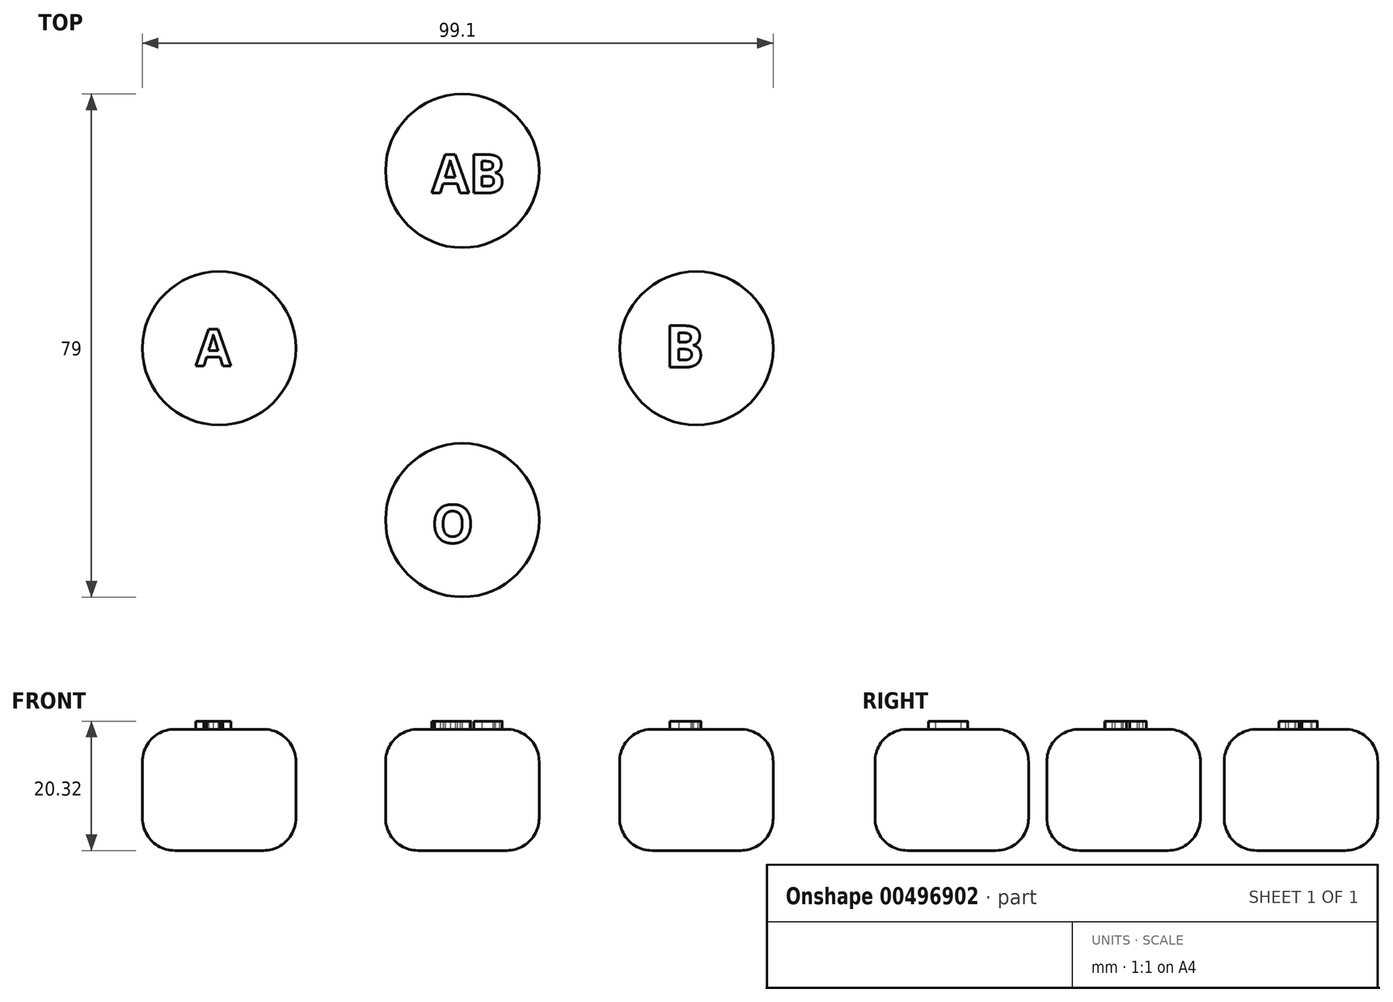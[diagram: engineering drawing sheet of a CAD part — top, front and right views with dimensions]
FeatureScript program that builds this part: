
annotation { "Feature Type Name" : "Feature", "Feature Type Description" : "" }
export const myFeature = defineFeature(function(context is Context, id is Id, definition is map)
    precondition{}
    {
        {
            var Q0;
            Q0=qCreatedBy(makeId("Top.planeOp"),FACE);
            var sketch = newSketch(context, id + "F0", { "sketchPlane" : qUnion([Q0])});
            skCircle(sketch, "E0", {"center": v(0, -27) * mm, "radius": 12.07 * mm});
            skCircle(sketch, "E1", {"center": v(36.77, 0) * mm, "radius": 12.07 * mm});
            skCircle(sketch, "E2", {"center": v(0, 27.86) * mm, "radius": 12.07 * mm});
            skCircle(sketch, "E3", {"center": v(-38.2, 0) * mm, "radius": 12.07 * mm});
            skSolve(sketch);
        }
        {
            var Q0;
            Q0 = qSketchRegion(id + "F0", true);
            extrude(context, id + "F1", {"entities" : qUnion([Q0]), "depth" : 19.05 * mm});
        }
        {
            var Q0;
            Q0=makeQuery(id+"F1.opExtrude","CAP_EDGE",EDGE,{"disambiguationData":[OSD([sQuery(id+"F0.wireOp",EDGE,"E3")])],"isStart":false});
            var Q1;
            Q1=makeQuery(id+"F1.opExtrude","CAP_EDGE",EDGE,{"disambiguationData":[OSD([sQuery(id+"F0.wireOp",EDGE,"E2")])],"isStart":false});
            var Q2;
            Q2=makeQuery(id+"F1.opExtrude","CAP_EDGE",EDGE,{"disambiguationData":[OSD([sQuery(id+"F0.wireOp",EDGE,"E1")])],"isStart":false});
            var Q3;
            Q3=makeQuery(id+"F1.opExtrude","CAP_EDGE",EDGE,{"disambiguationData":[OSD([sQuery(id+"F0.wireOp",EDGE,"E0")])],"isStart":false});
            var Q4;
            Q4=makeQuery(id+"F1.opExtrude","CAP_EDGE",EDGE,{"disambiguationData":[OSD([sQuery(id+"F0.wireOp",EDGE,"E0")])],"isStart":true});
            var Q5;
            Q5=makeQuery(id+"F1.opExtrude","CAP_EDGE",EDGE,{"disambiguationData":[OSD([sQuery(id+"F0.wireOp",EDGE,"E1")])],"isStart":true});
            var Q6;
            Q6=makeQuery(id+"F1.opExtrude","CAP_EDGE",EDGE,{"disambiguationData":[OSD([sQuery(id+"F0.wireOp",EDGE,"E2")])],"isStart":true});
            var Q7;
            Q7=makeQuery(id+"F1.opExtrude","CAP_EDGE",EDGE,{"disambiguationData":[OSD([sQuery(id+"F0.wireOp",EDGE,"E3")])],"isStart":true});
            fillet(context, id + "F2", {"entities" : qUnion([Q0, Q1, Q2, Q3, Q4, Q5, Q6, Q7]), "radius" : 5.08 * mm, "tangentPropagation" : true, "allowEdgeOverflow" : false});
        }
        {
            var Q0;
            Q0=makeQuery(id+"F1.opExtrude","CAP_FACE",FACE,{"disambiguationData":[OSD([sQuery(id+"F0.wireOp",EDGE,"E3")])],"isStart":false});
            var sketch = newSketch(context, id + "F3", { "sketchPlane" : qUnion([Q0])});
            skText(sketch, "E4", { "text": "A", "fontName": "OpenSans-Bold.ttf"});
            const initialGuessF3  = {"E4": [-0.0419, -0.00276, 1, 0, 0.0058]};
            skSetInitialGuess(sketch, initialGuessF3);
            skSolve(sketch);
        }
        {
            var Q0;
            Q0 = qSketchRegion(id + "F3", true);
            extrude(context, id + "F4", {"entities" : qUnion([Q0]), "operationType" : NewBodyOperationType.ADD, "depth" : 1.27 * mm});
        }
        {
            var Q0;
            Q0=makeQuery(id+"F1.opExtrude","CAP_FACE",FACE,{"disambiguationData":[OSD([sQuery(id+"F0.wireOp",EDGE,"E2")])],"isStart":false});
            var sketch = newSketch(context, id + "F5", { "sketchPlane" : qUnion([Q0])});
            skText(sketch, "E5", { "text": "AB", "fontName": "OpenSans-Bold.ttf"});
            const initialGuessF5  = {"E5": [-0.00482, 0.02439, 1, 0, 0.0061]};
            skSetInitialGuess(sketch, initialGuessF5);
            skSolve(sketch);
        }
        {
            var Q0;
            Q0 = qSketchRegion(id + "F5", true);
            extrude(context, id + "F6", {"entities" : qUnion([Q0]), "operationType" : NewBodyOperationType.ADD, "depth" : 1.27 * mm});
        }
        {
            var Q0;
            Q0=makeQuery(id+"F1.opExtrude","CAP_FACE",FACE,{"disambiguationData":[OSD([sQuery(id+"F0.wireOp",EDGE,"E0")])],"isStart":false});
            var sketch = newSketch(context, id + "F7", { "sketchPlane" : qUnion([Q0])});
            skText(sketch, "E6", { "text": "O\n", "fontName": "OpenSans-Bold.ttf"});
            const initialGuessF7  = {"E6": [-0.00483, -0.03056, 1, 0, 0.00599]};
            skSetInitialGuess(sketch, initialGuessF7);
            skSolve(sketch);
        }
        {
            var Q0;
            Q0 = qSketchRegion(id + "F7", true);
            extrude(context, id + "F8", {"entities" : qUnion([Q0]), "operationType" : NewBodyOperationType.ADD, "depth" : 1.27 * mm});
        }
        {
            var Q0;
            Q0=makeQuery(id+"F1.opExtrude","CAP_FACE",FACE,{"disambiguationData":[OSD([sQuery(id+"F0.wireOp",EDGE,"E1")])],"isStart":false});
            var sketch = newSketch(context, id + "F9", { "sketchPlane" : qUnion([Q0])});
            skText(sketch, "E7", { "text": "B", "fontName": "OpenSans-Bold.ttf"});
            const initialGuessF9  = {"E7": [0.0318, -0.00298, 1, 0, 0.00659]};
            skSetInitialGuess(sketch, initialGuessF9);
            skSolve(sketch);
        }
        {
            var Q0;
            Q0 = qSketchRegion(id + "F9", true);
            extrude(context, id + "F10", {"entities" : qUnion([Q0]), "operationType" : NewBodyOperationType.ADD, "depth" : 1.27 * mm});
        }
    });
